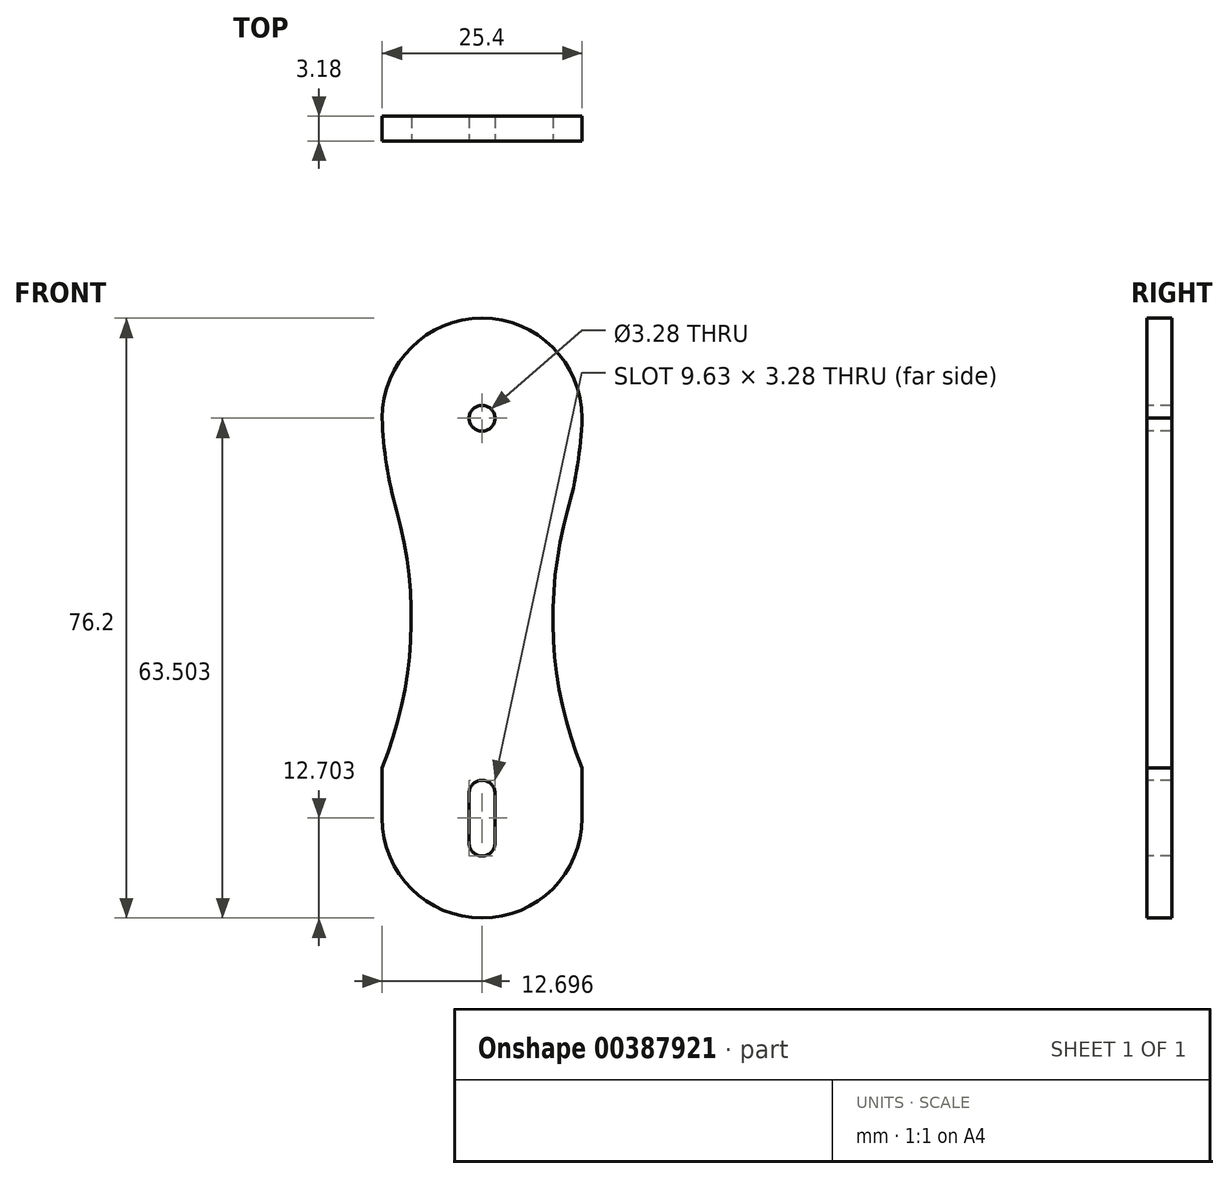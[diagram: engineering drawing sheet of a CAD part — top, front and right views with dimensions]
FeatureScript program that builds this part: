
annotation { "Feature Type Name" : "Feature", "Feature Type Description" : "" }
export const myFeature = defineFeature(function(context is Context, id is Id, definition is map)
    precondition{}
    {
        {
            var Q0;
            Q0=qCreatedBy(makeId("Front.planeOp"),FACE);
            var sketch = newSketch(context, id + "F0", { "sketchPlane" : qUnion([Q0])});
            skLineSegment(sketch, "E0.bottom", {"start": v(-27.75, -35.58) * mm, "end": v(-2.35, -35.58) * mm});
            skLineSegment(sketch, "E0.top", {"start": v(-27.75, 40.62) * mm, "end": v(-2.35, 40.62) * mm});
            skLineSegment(sketch, "E0.left", {"start": v(-27.75, -35.58) * mm, "end": v(-27.75, 40.62) * mm});
            skLineSegment(sketch, "E0.right", {"start": v(-2.35, -35.58) * mm, "end": v(-2.35, 40.62) * mm});
            skSolve(sketch);
        }
        {
            var Q0;
            Q0 = qSketchRegion(id + "F0", true);
            extrude(context, id + "F1", {"entities" : qUnion([Q0]), "depth" : 3.17 * mm});
        }
        {
            var Q0;
            Q0=makeQuery(id+"F1.opExtrude","CAP_FACE",FACE,{"disambiguationData":[OSD([sQuery(id+"F0.wireOp",EDGE,"E0.bottom"),sQuery(id+"F0.wireOp",EDGE,"E0.top"),sQuery(id+"F0.wireOp",EDGE,"E0.left"),sQuery(id+"F0.wireOp",EDGE,"E0.right")])],"isStart":false});
            var sketch = newSketch(context, id + "F2", { "sketchPlane" : qUnion([Q0])});
            skLineSegment(sketch, "E1", {"start": v(-2.35, -22.8) * mm, "end": v(-27.75, -22.8) * mm, "construction": true});
            skLineSegment(sketch, "E2", {"start": v(-2.35, 27.92) * mm, "end": v(-27.75, 27.92) * mm, "construction": true});
            skCircle(sketch, "E3", {"center": v(-15.05, 27.92) * mm, "radius": 1.64 * mm});
            skLineSegment(sketch, "E4", {"start": v(-15.05, -19.7) * mm, "end": v(-15.05, -26.05) * mm});
            skArc(sketch, "E5.0.startCap", {"start": v(-16.7, -19.7) * mm, "mid": v(-15.05, -18.06) * mm, "end": v(-13.42, -19.7) * mm});
            skArc(sketch, "E5.0.endCap", {"start": v(-13.42, -26.05) * mm, "mid": v(-15.05, -27.7) * mm, "end": v(-16.7, -26.05) * mm});
            skLineSegment(sketch, "E5.0.left", {"start": v(-13.42, -19.7) * mm, "end": v(-13.42, -26.05) * mm});
            skLineSegment(sketch, "E5.0.right", {"start": v(-16.7, -19.7) * mm, "end": v(-16.7, -26.05) * mm});
            skSolve(sketch);
        }
        {
            var Q0;
            Q0 = qSketchRegion(id + "F2", true);
            extrude(context, id + "F3", {"entities" : qUnion([Q0]), "operationType" : NewBodyOperationType.REMOVE, "oppositeDirection" : true, "depth" : 25.4 * mm});
        }
        {
            var Q0;
            Q0=makeQuery(id+"F1.opExtrude","SWEPT_EDGE",EDGE,{"disambiguationData":[OSD([sQuery(id+"F0.wireOp",EDGE,"E0.bottom"),sQuery(id+"F0.wireOp",EDGE,"E0.right")])]});
            var Q1;
            Q1=makeQuery(id+"F1.opExtrude","SWEPT_EDGE",EDGE,{"disambiguationData":[OSD([sQuery(id+"F0.wireOp",EDGE,"E0.bottom"),sQuery(id+"F0.wireOp",EDGE,"E0.left")])]});
            var Q2;
            Q2=makeQuery(id+"F1.opExtrude","SWEPT_EDGE",EDGE,{"disambiguationData":[OSD([sQuery(id+"F0.wireOp",EDGE,"E0.top"),sQuery(id+"F0.wireOp",EDGE,"E0.left")])]});
            var Q3;
            Q3=makeQuery(id+"F1.opExtrude","SWEPT_EDGE",EDGE,{"disambiguationData":[OSD([sQuery(id+"F0.wireOp",EDGE,"E0.top"),sQuery(id+"F0.wireOp",EDGE,"E0.right")])]});
            fillet(context, id + "F4", {"entities" : qUnion([Q0, Q1, Q2, Q3]), "radius" : 12.7 * mm, "tangentPropagation" : true, "allowEdgeOverflow" : false});
        }
        {
            var Q0;
            Q0=makeQuery(id+"F1.opExtrude","CAP_FACE",FACE,{"disambiguationData":[OSD([sQuery(id+"F0.wireOp",EDGE,"E0.bottom"),sQuery(id+"F0.wireOp",EDGE,"E0.top"),sQuery(id+"F0.wireOp",EDGE,"E0.left"),sQuery(id+"F0.wireOp",EDGE,"E0.right")])],"isStart":false});
            var sketch = newSketch(context, id + "F5", { "sketchPlane" : qUnion([Q0])});
            skLineSegment(sketch, "E6", {"start": v(-27.75, 21.57) * mm, "end": v(-2.35, 21.57) * mm, "construction": true});
            skLineSegment(sketch, "E7", {"start": v(-27.75, -16.53) * mm, "end": v(-2.35, -16.53) * mm, "construction": true});
            skArc(sketch, "E8", {"start": v(-27.75, -16.53) * mm, "mid": v(-24.05, 2.52) * mm, "end": v(-27.75, 21.57) * mm});
            skArc(sketch, "E9", {"start": v(-2.35, 21.57) * mm, "mid": v(-6.06, 2.52) * mm, "end": v(-2.35, -16.53) * mm});
            skLineSegment(sketch, "E10", {"start": v(-2.35, 21.57) * mm, "end": v(-2.35, -16.53) * mm});
            skLineSegment(sketch, "E11", {"start": v(-27.75, 21.57) * mm, "end": v(-27.75, -16.53) * mm});
            skSolve(sketch);
        }
        {
            var Q0;
            Q0 = qSketchRegion(id + "F5", true);
            extrude(context, id + "F6", {"entities" : qUnion([Q0]), "operationType" : NewBodyOperationType.REMOVE, "oppositeDirection" : true, "depth" : 25.4 * mm});
        }
        {
            var Q0;
            {var subQ0=sQuery(id+"F5.wireOp",EDGE,"E11");var subQ1=sQuery(id+"F5.wireOp",EDGE,"E8");var subQ2=sQuery(id+"F0.wireOp",EDGE,"E0.left");Q0=makeQuery(id+"F6.boolean.opBoolean","COPY",EDGE,{"derivedFrom":makeQuery(id+"F6.opExtrude","SWEPT_EDGE",EDGE,{"disambiguationData":[OSD([subQ2,subQ1,subQ0]),TDD([makeQuery(id+"F5.imprint","INTERSECT",VERTEX,{"disambiguationData":[OD(1.0)],"derivedFrom":[makeQuery(id+"F1.opExtrude","CAP_EDGE",EDGE,{"disambiguationData":[OSD([subQ2])],"isStart":false}),subQ1,subQ0]})])]})});}
            var Q1;
            {var subQ0=sQuery(id+"F5.wireOp",EDGE,"E11");var subQ1=sQuery(id+"F5.wireOp",EDGE,"E8");var subQ2=sQuery(id+"F0.wireOp",EDGE,"E0.left");Q1=makeQuery(id+"F6.boolean.opBoolean","COPY",EDGE,{"derivedFrom":makeQuery(id+"F6.opExtrude","SWEPT_EDGE",EDGE,{"disambiguationData":[OSD([subQ2,subQ1,subQ0]),TDD([makeQuery(id+"F5.imprint","INTERSECT",VERTEX,{"disambiguationData":[OD(0.0)],"derivedFrom":[makeQuery(id+"F1.opExtrude","CAP_EDGE",EDGE,{"disambiguationData":[OSD([subQ2])],"isStart":false}),subQ1,subQ0]})])]})});}
            var Q2;
            {var subQ0=sQuery(id+"F5.wireOp",EDGE,"E10");var subQ1=sQuery(id+"F5.wireOp",EDGE,"E9");var subQ2=sQuery(id+"F0.wireOp",EDGE,"E0.right");Q2=makeQuery(id+"F6.boolean.opBoolean","COPY",EDGE,{"derivedFrom":makeQuery(id+"F6.opExtrude","SWEPT_EDGE",EDGE,{"disambiguationData":[OSD([subQ2,subQ1,subQ0]),TDD([makeQuery(id+"F5.imprint","INTERSECT",VERTEX,{"disambiguationData":[OD(1.0)],"derivedFrom":[makeQuery(id+"F1.opExtrude","CAP_EDGE",EDGE,{"disambiguationData":[OSD([subQ2])],"isStart":false}),subQ1,subQ0]})])]})});}
            var Q3;
            {var subQ0=sQuery(id+"F5.wireOp",EDGE,"E10");var subQ1=sQuery(id+"F5.wireOp",EDGE,"E9");var subQ2=sQuery(id+"F0.wireOp",EDGE,"E0.right");Q3=makeQuery(id+"F6.boolean.opBoolean","COPY",EDGE,{"derivedFrom":makeQuery(id+"F6.opExtrude","SWEPT_EDGE",EDGE,{"disambiguationData":[OSD([subQ2,subQ1,subQ0]),TDD([makeQuery(id+"F5.imprint","INTERSECT",VERTEX,{"disambiguationData":[OD(0.0)],"derivedFrom":[makeQuery(id+"F1.opExtrude","CAP_EDGE",EDGE,{"disambiguationData":[OSD([subQ2])],"isStart":false}),subQ1,subQ0]})])]})});}
            fillet(context, id + "F7", {"entities" : qUnion([Q0, Q1, Q2, Q3]), "radius" : 50.8 * mm, "tangentPropagation" : true, "allowEdgeOverflow" : false});
        }
    });
